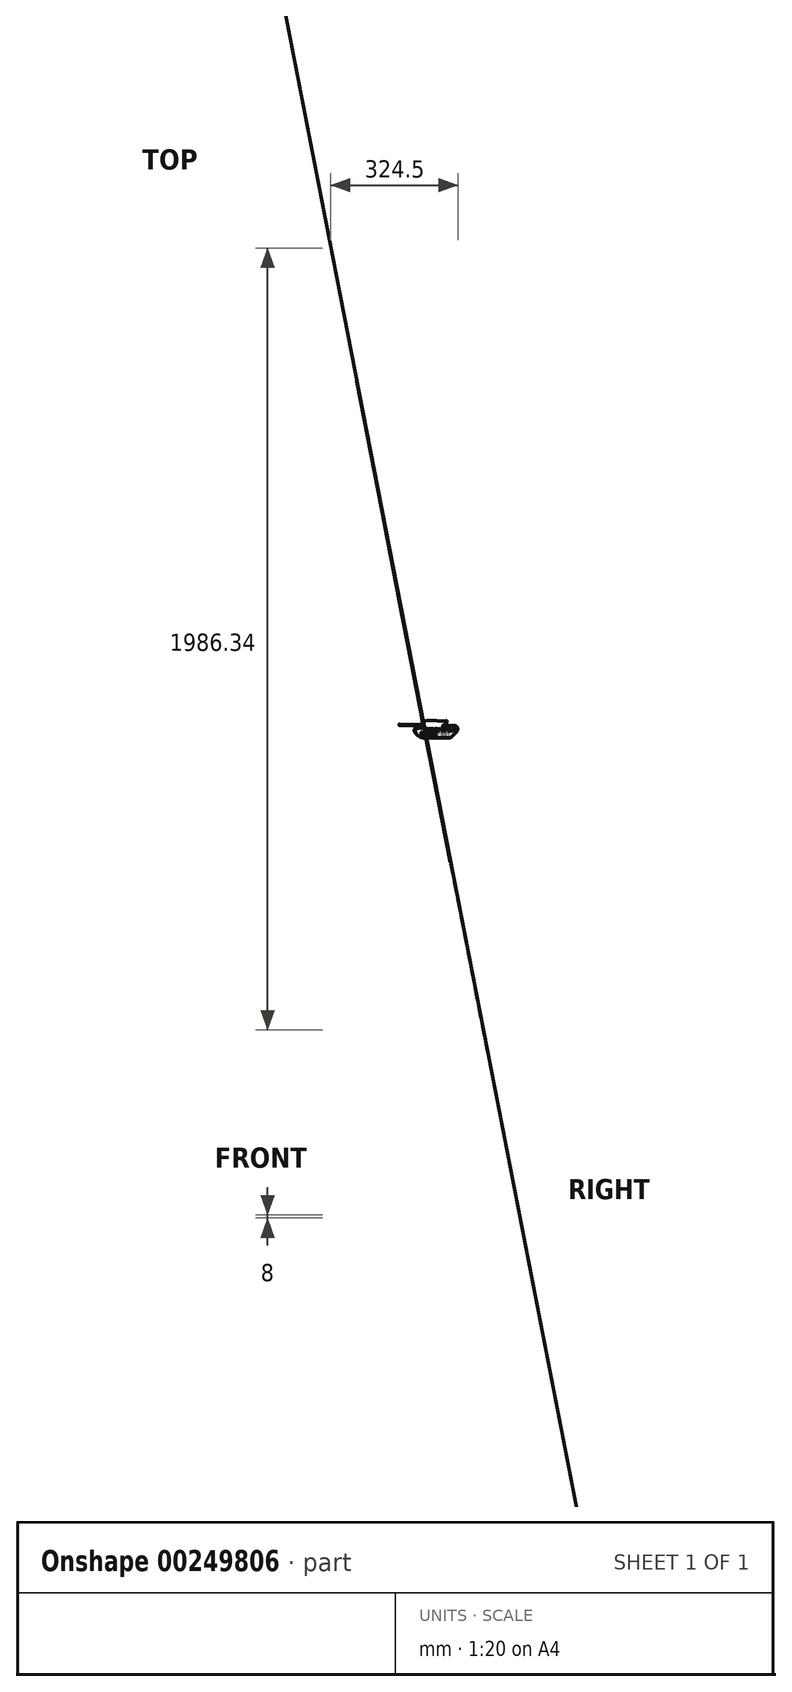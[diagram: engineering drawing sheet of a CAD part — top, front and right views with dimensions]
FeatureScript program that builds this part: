
annotation { "Feature Type Name" : "Feature", "Feature Type Description" : "" }
export const myFeature = defineFeature(function(context is Context, id is Id, definition is map)
    precondition{}
    {
        {
            var Q0;
            Q0=qCreatedBy(makeId("Top.planeOp"),FACE);
            var sketch = newSketch(context, id + "F0", { "sketchPlane" : qUnion([Q0])});
            skFitSpline(sketch, "E0", {"points": [v(-71.87, 9.46) * mm, v(-72.2, 6.14) * mm, v(-71.54, 5.73) * mm, v(-16.62, 5.32) * mm, v(-12.23, 4.49) * mm, v(-12.57, 3.9) * mm, v(-12.32, 2.83) * mm, v(-8.42, 1.67) * mm, v(-8.59, 0.76) * mm, v(-11.9, 1.1) * mm, v(-14.88, 0.68) * mm, v(-15.63, 0) * mm, v(-19.52, -1.06) * mm, v(-28.3, -1.23) * mm, v(-35.34, -5.78) * mm, v(-32.03, -11.58) * mm, v(-29.05, -15.97) * mm, v(-14.36, -25.79) * mm, v(-5.86, -26.08) * mm, v(57.94, -25.64) * mm, v(60.26, -24.31) * mm, v(74.84, -10.26) * mm, v(78, -3) * mm, v(74.25, 0) * mm, v(74.37, 4.03) * mm, v(67.7, 5.67) * mm, v(66.52, 4.85) * mm, v(61.95, 5.55) * mm, v(48.83, 5.55) * mm, v(39.11, 3.2) * mm, v(35.86, 4.08) * mm, v(46.02, 6.72) * mm, v(46.6, 9.42) * mm, v(50.7, 10.12) * mm, v(49.61, 18.09) * mm, v(48.87, 18.09) * mm, v(43.15, 18.32) * mm, v(5.43, 19.2) * mm, v(-2.83, 19.14) * mm, v(-7.1, 17.71) * mm, v(-10.33, 15.23) * mm, v(-9.46, 12) * mm, v(-10.98, 9.84) * mm, v(-14.16, 9.51) * mm, v(-70.2, 9.51) * mm, v(-71.87, 9.46) * mm]});
            skSolve(sketch);
        }
        {
            var Q0;
            Q0=makeQuery(id+"F0.imprint","IMPRINT",FACE,{"disambiguationData":[TD([[makeQuery(id+"F0.imprint","IMPRINT",EDGE,{"derivedFrom":sQuery(id+"F0.wireOp",EDGE,"E0")}),1.0]])]});
            extrude(context, id + "F1", {"entities" : qUnion([Q0]), "depth" : 5 * mm});
        }
        {
            var Q0;
            Q0=qCreatedBy(makeId("Top.planeOp"),FACE);
            var sketch = newSketch(context, id + "F2", { "sketchPlane" : qUnion([Q0])});
            skText(sketch, "E1", { "text": "םיקעוצ 16 \'גוא", "fontName": "Arimo-Bold.ttf"});
            skText(sketch, "E2", { "text": "!וליצה", "fontName": "Arimo-Bold.ttf"});
            const initialGuessF2  = {"E1": [-0.00518, -0.00815, 1, 0, 0.00815], "E2": [-0.01788, -0.02095, 1, 0, 0.01035]};
            skSetInitialGuess(sketch, initialGuessF2);
            skSolve(sketch);
        }
        {
            var Q0;
            Q0 = qSketchRegion(id + "F2", true);
            extrude(context, id + "F3", {"entities" : qUnion([Q0]), "operationType" : NewBodyOperationType.ADD, "depth" : 8 * mm});
        }
        {
            var Q0;
            Q0=makeQuery(id+"F1.opExtrude","CAP_EDGE",EDGE,{"disambiguationData":[OSD([sQuery(id+"F0.wireOp",EDGE,"E0")])],"isStart":false});
            var Q1;
            Q1=makeQuery(id+"F1.opExtrude","SWEPT_FACE",FACE,{"disambiguationData":[OSD([sQuery(id+"F0.wireOp",EDGE,"E0")])]});
            fillet(context, id + "F4", {"entities" : qUnion([Q0, Q1]), "radius" : 1 * mm, "tangentPropagation" : true, "allowEdgeOverflow" : false});
        }
        {
            var Q0;
            Q0=makeQuery(id+"F1.opExtrude","CAP_FACE",FACE,{"disambiguationData":[OSD([sQuery(id+"F0.wireOp",EDGE,"E0")])],"isStart":true});
            var sketch = newSketch(context, id + "F5", { "sketchPlane" : qUnion([Q0])});
            skText(sketch, "E3", { "text": "דרעמ ךלמה ודיעל", "fontName": "Arimo-Bold.ttf"});
            const initialGuessF5  = {"E3": [0.058, 0.01649, -1, 0, 0.007]};
            skSetInitialGuess(sketch, initialGuessF5);
            skSolve(sketch);
        }
        {
            var Q0;
            Q0 = qSketchRegion(id + "F5", true);
            extrude(context, id + "F6", {"entities" : qUnion([Q0]), "operationType" : NewBodyOperationType.REMOVE, "oppositeDirection" : true, "depth" : 2 * mm});
        }
    });
